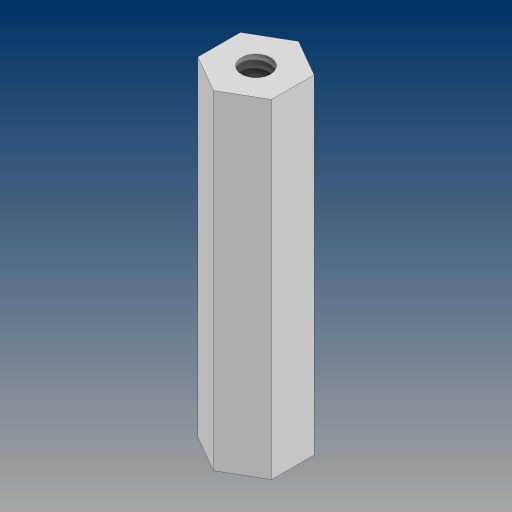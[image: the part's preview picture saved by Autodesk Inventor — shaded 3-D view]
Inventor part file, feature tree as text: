
AUTODESK INVENTOR PART (.ipt)
format: ipt  version: 2024.3 (Build 283343000, 343)  size: 96,256 bytes
history: native  units: in
note: dims shown in document units (in); Inventor stores cm internally (conversion verified against a paired STEP export)
features: sketch x2, extrude x1, hole x1
ambient origin geometry x8: Origin, YZ Plane, XZ Plane, XY Plane, X Axis, Y Axis, Z Axis, Center Point
bodies: Solid1 (feature_tree)
feature tree (4):
  extrude  "Extrusion1"  Depth=2.233in TaperAngle=0.0deg
  hole  "Hole1"  [1 undecoded]
  sketch  "Sketch1"  dims[d0=0.5in d1=2.233in d2=0.0in]
  sketch  "Sketch2"  dims[d3=0.196in d4=1.0in d5=0.375in d6=0.25in d7=0.5635in d8=1.0in d9=0.8108in]
note: 1 required parameter value undecoded (feature->parameter linkage not recoverable at this tier; creation-order binding heuristic only, values carry confidence <= 0.55)
